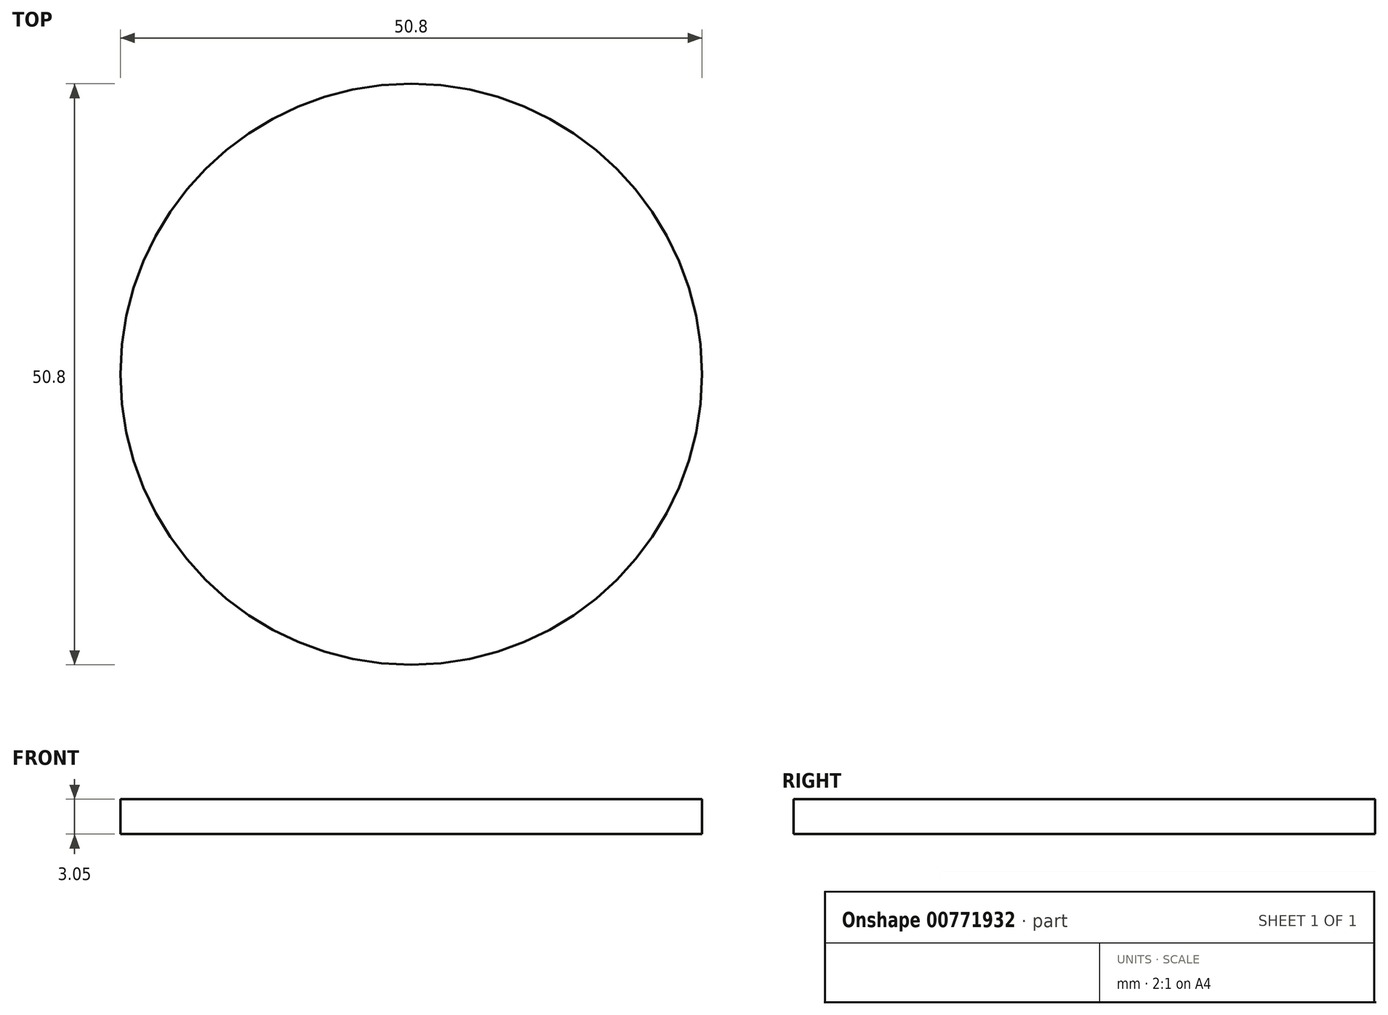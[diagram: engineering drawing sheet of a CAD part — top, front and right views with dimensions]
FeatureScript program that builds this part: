
annotation { "Feature Type Name" : "Feature", "Feature Type Description" : "" }
export const myFeature = defineFeature(function(context is Context, id is Id, definition is map)
    precondition{}
    {
        {
            var Q0;
            Q0=qCreatedBy(makeId("Top.planeOp"),FACE);
            var sketch = newSketch(context, id + "F0", { "sketchPlane" : qUnion([Q0])});
            skCircle(sketch, "E0", {"center": v(0, 0) * mm, "radius": 25.4 * mm});
            skSolve(sketch);
        }
        {
            var Q0;
            Q0 = qSketchRegion(id + "F0", true);
            extrude(context, id + "F1", {"entities" : qUnion([Q0]), "depth" : 3.05 * mm, "offsetDistance" : 25.4 * mm});
        }
    });
